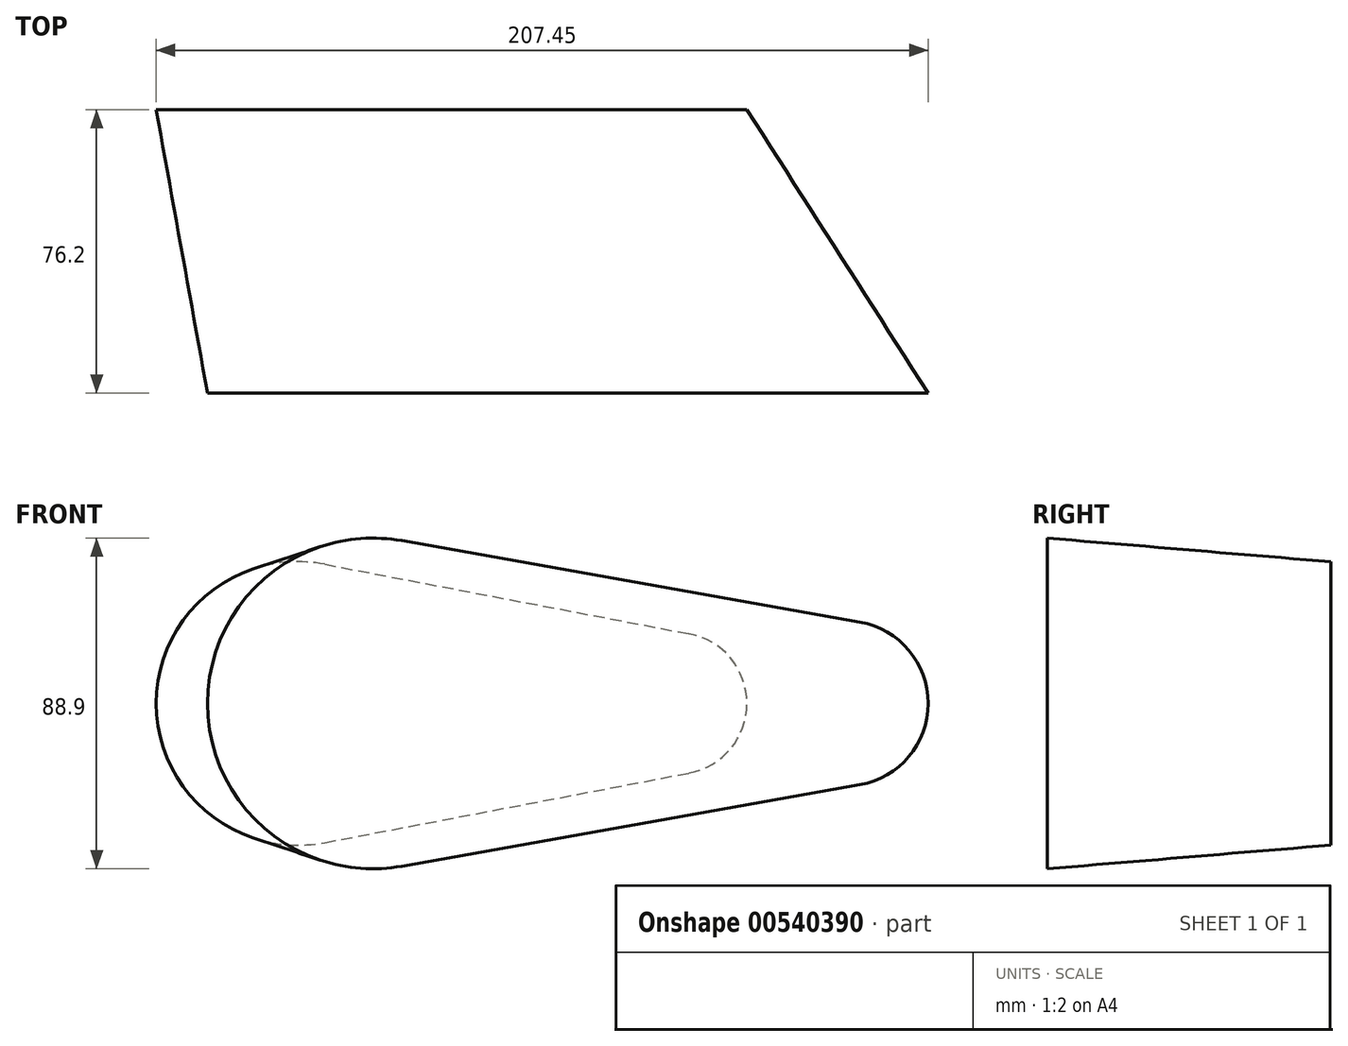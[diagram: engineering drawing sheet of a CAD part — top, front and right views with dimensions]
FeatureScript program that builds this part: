
annotation { "Feature Type Name" : "Feature", "Feature Type Description" : "" }
export const myFeature = defineFeature(function(context is Context, id is Id, definition is map)
    precondition{}
    {
        {
            var Q0;
            Q0=qCreatedBy(makeId("Front.planeOp"),FACE);
            var sketch = newSketch(context, id + "F0", { "sketchPlane" : qUnion([Q0])});
            skArc(sketch, "E0", {"start": v(-56.36, 37.42) * mm, "mid": v(-101.6, 0) * mm, "end": v(-56.36, -37.42) * mm});
            skArc(sketch, "E1", {"start": v(41.67, -18.71) * mm, "mid": v(57.15, 0) * mm, "end": v(41.67, 18.71) * mm});
            skLineSegment(sketch, "E2", {"start": v(-56.36, 37.42) * mm, "end": v(41.67, 18.71) * mm});
            skLineSegment(sketch, "E3", {"start": v(-86.23, 0) * mm, "end": v(99.03, 0) * mm, "construction": true});
            skLineSegment(sketch, "E4.MirrorCS", {"start": v(-56.36, -37.42) * mm, "end": v(41.67, -18.71) * mm});
            skCircle(sketch, "E5", {"center": v(-63.5, 0) * mm, "radius": 25.4 * mm, "construction": true});
            skCircle(sketch, "E6", {"center": v(38.1, 0) * mm, "radius": 12.7 * mm, "construction": true});
            skSolve(sketch);
        }
        {
            var Q0;
            Q0=qCreatedBy(makeId("Front.planeOp"),FACE);
            cPlane(context, id + "F1", {"entities" : qUnion([Q0]), "cplaneType" : CPlaneType.OFFSET, "offset" : 76.2 * mm, "width" : 152.4 * mm, "height" : 152.4 * mm});
        }
        {
            var Q0;
            Q0=qCreatedBy(id+"F1.planeOp",FACE);
            var sketch = newSketch(context, id + "F2", { "sketchPlane" : qUnion([Q0])});
            skArc(sketch, "E7", {"start": v(-35.6, 43.76) * mm, "mid": v(-87.83, 0) * mm, "end": v(-35.6, -43.76) * mm});
            skArc(sketch, "E8", {"start": v(87.51, -21.88) * mm, "mid": v(105.85, 0) * mm, "end": v(87.51, 21.88) * mm});
            skLineSegment(sketch, "E9", {"start": v(-35.6, 43.76) * mm, "end": v(87.51, 21.88) * mm});
            skLineSegment(sketch, "E10", {"start": v(-77.8, 0) * mm, "end": v(107.48, 0) * mm, "construction": true});
            skLineSegment(sketch, "E11.MirrorCS", {"start": v(-35.6, -43.76) * mm, "end": v(87.51, -21.88) * mm});
            skCircle(sketch, "E12", {"center": v(-43.38, 0) * mm, "radius": 31.75 * mm, "construction": true});
            skCircle(sketch, "E13", {"center": v(83.62, 0) * mm, "radius": 15.88 * mm, "construction": true});
            skSolve(sketch);
        }
        {
            var Q0;
            Q0=qCreatedBy(makeId("Front.planeOp"),FACE);
            cPlane(context, id + "F3", {"entities" : qUnion([Q0]), "cplaneType" : CPlaneType.OFFSET, "offset" : 12.7 * mm, "oppositeDirection" : true, "width" : 152.4 * mm, "height" : 152.4 * mm});
        }
        {
            var Q0;
            Q0=makeQuery(id+"F0.imprint","IMPRINT",FACE,{"disambiguationData":[TD([[makeQuery(id+"F0.imprint","IMPRINT",EDGE,{"derivedFrom":sQuery(id+"F0.wireOp",EDGE,"E0")}),1.0]])]});
            var Q1;
            Q1=makeQuery(id+"F2.imprint","IMPRINT",FACE,{"disambiguationData":[TD([[makeQuery(id+"F2.imprint","IMPRINT",EDGE,{"derivedFrom":sQuery(id+"F2.wireOp",EDGE,"E7")}),1.0]])]});
            loft(context, id + "F4", {"sheetProfilesArray" : [{ "sheetProfileEntities" : qUnion([Q0]) }, { "sheetProfileEntities" : qUnion([Q1]) }]});
        }
    });
